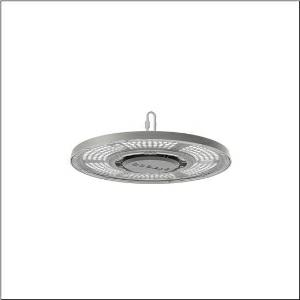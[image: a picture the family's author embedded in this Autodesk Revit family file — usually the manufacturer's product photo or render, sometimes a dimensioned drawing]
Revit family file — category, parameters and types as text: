
# Revit family: highbay_31-s_51hc41da4fmb
name_source: partatom
category: Lighting Fixtures
units: mm (PartAtom-declared; Revit-internal decimal feet)

## family parameters
Cut with Voids When Loaded = No
Host = Face
Light Source = No
Part Type = Normal
Room Calculation Point = No
Round Connector Dimension = Use Diameter
Shared = No

## types (1)
- Highbay 31-S (1 x LED, 14000 lm, 94 W, 4000K)
    Apparent Load = 94 VA
    CIE Flux Codes = 94 98 100 100 100
    Color Rendering = 80
    Color Temperature = 4000K
    Default Elevation = 1800 mm
    Description = Highbay 31-S, high bay luminaire, primary light control with lens, of PC, primary optical cover: cover panel, of PC, transparent, light emission: direct distribution, primary light characteristic: rotationally symmetric, installation type: suspended mounting, surface-mounted, LED, rated luminous flux: 14.000lm, luminous efficacy: 150lm/W, light colour: 840, colour temperature: 4000K, control gear: DALI 2, with cable, 5x 1.0mm², free wire ends, mains connection: 220..240V, AC/DC, 0/50..60Hz, cable length: 1,5m, rated input power: 94W, housing, rotationally symmetric, of diecast aluminium, powder-coated, grey aluminium (RAL 9007), with hook on luminaire side, incl. screw, diameter: 339mm, protection rating (complete): IP65, insulation class (complete): insulation class I (protective earthing), certification: CE, ENEC, UKCA, protection symbol: D, impact resistance: IK08, permissible operating ambient temperature: -30..+45°C, standard: EN 60598-2-22, EN 60598, corresponds to IFS (International Featured Standards) requirements for safety and quality in the food industry, packaging unit: 1 piece
    Height = 141 mm
    Lamp = 1 x LED
    Lamp Light Flux = 14000 lm
    Lamp Power = 94 W
    Lamp count = 1
    Length = 339 mm
    Luminous efficacy = 149 lm/W
    Manufacturer = Siteco
    ModVariant = No
    Model = 51HC41DA4FMB
    Mounting Place = Ceiling
    Mounting Type = Pendant
    Number of Poles = 1
    OnlyDefault = Yes
    Power Factor = 1
    Product Name = Highbay 31-S
    Product group = high bay luminaire
    ProductGroupID = 901
    Protection Class = Protection class I
    Protection Degree = IP 65
    RLX_Detail_Level = 1
    RLX_Emergency_Light_Flux = 0 lm
    RLX_Emergency_Type = 0
    RLX_Emergency_Type_DB = No
    RlxData = <blob elided: 107405 chars, md5=53312c48>
    Socket = socket
    Standby Power = 0 W
    System Light Flux = 14000 lm
    System Power = 94 W
    Type Comments = Product without accessories
    Type Image = l_1007237.jpg
    URL = http://relux.com
    VarID = ---
    Voltage = 0 V
    Weight = 0.00 kg
    Width = 0 mm  [stored 0 ft]

note: [stored X ft] marks values corroborated as IEEE doubles in the binary element streams (Revit-internal decimal feet)

## geometry (parser evidence)
native form markers: Blend x4, Sweep x9
no freeform markers — native parametric forms only
